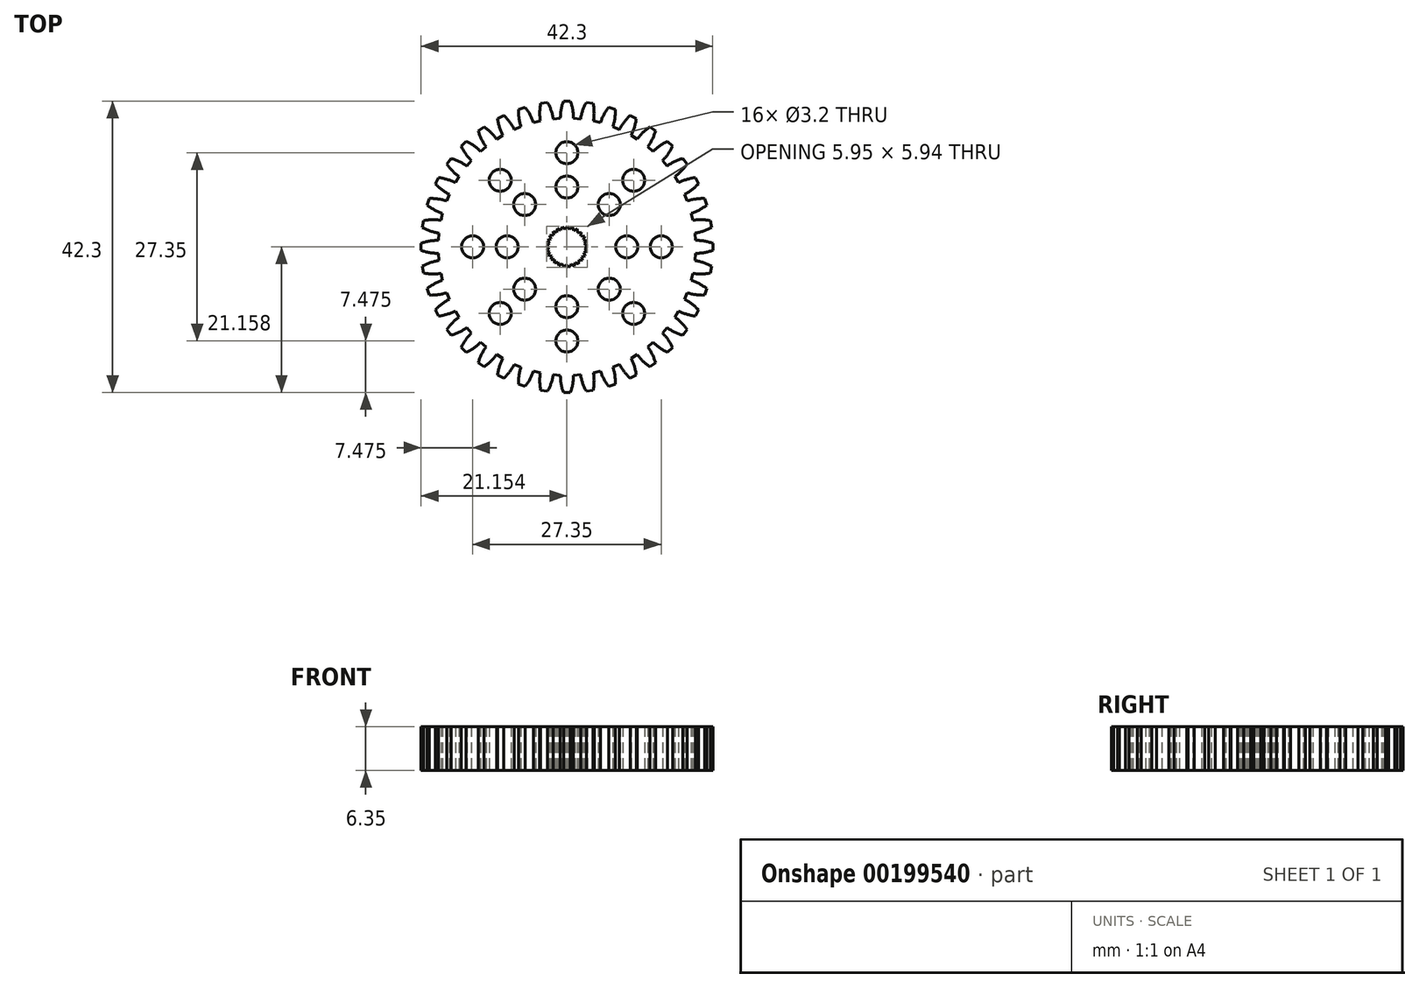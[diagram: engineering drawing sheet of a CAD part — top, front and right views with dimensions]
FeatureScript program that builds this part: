
annotation { "Feature Type Name" : "Feature", "Feature Type Description" : "" }
export const myFeature = defineFeature(function(context is Context, id is Id, definition is map)
    precondition{}
    {
        {
            var Q0;
            Q0=qCreatedBy(makeId("Top.planeOp"),FACE);
            var sketch = newSketch(context, id + "F0", { "sketchPlane" : qUnion([Q0])});
            skLineSegment(sketch, "E0", {"start": v(-0.5, 21.15) * mm, "end": v(0.5, 21.15) * mm});
            skArc(sketch, "E1", {"start": v(-0.5, 21.15) * mm, "mid": v(-0.84, 19.92) * mm, "end": v(-0.95, 18.65) * mm});
            skArc(sketch, "E2.MirrorCS", {"start": v(0.5, 21.15) * mm, "mid": v(0.84, 19.92) * mm, "end": v(0.95, 18.65) * mm});
            skArc(sketch, "E3.1.0", {"start": v(-2.81, 20.97) * mm, "mid": v(-2.3, 19.8) * mm, "end": v(-1.98, 18.57) * mm});
            skLineSegment(sketch, "E3.1.1", {"start": v(-3.8, 20.81) * mm, "end": v(-2.81, 20.97) * mm});
            skArc(sketch, "E3.1.2", {"start": v(-3.8, 20.81) * mm, "mid": v(-3.94, 19.54) * mm, "end": v(-3.86, 18.27) * mm});
            skArc(sketch, "E3.2.0", {"start": v(-6.06, 20.27) * mm, "mid": v(-5.36, 19.2) * mm, "end": v(-4.86, 18.03) * mm});
            skLineSegment(sketch, "E3.2.1", {"start": v(-7.01, 19.96) * mm, "end": v(-6.06, 20.27) * mm});
            skArc(sketch, "E3.2.2", {"start": v(-7.01, 19.96) * mm, "mid": v(-6.95, 18.69) * mm, "end": v(-6.67, 17.44) * mm});
            skArc(sketch, "E3.3.0", {"start": v(-9.16, 19.07) * mm, "mid": v(-8.3, 18.13) * mm, "end": v(-7.62, 17.05) * mm});
            skLineSegment(sketch, "E3.3.1", {"start": v(-10.05, 18.62) * mm, "end": v(-9.16, 19.07) * mm});
            skArc(sketch, "E3.3.2", {"start": v(-10.05, 18.62) * mm, "mid": v(-9.79, 17.37) * mm, "end": v(-9.31, 16.19) * mm});
            skArc(sketch, "E3.4.0", {"start": v(-12.03, 17.4) * mm, "mid": v(-11.03, 16.6) * mm, "end": v(-10.2, 15.65) * mm});
            skLineSegment(sketch, "E3.4.1", {"start": v(-12.84, 16.82) * mm, "end": v(-12.03, 17.4) * mm});
            skArc(sketch, "E3.4.2", {"start": v(-12.84, 16.82) * mm, "mid": v(-12.39, 15.62) * mm, "end": v(-11.73, 14.53) * mm});
            skArc(sketch, "E3.5.0", {"start": v(-14.6, 15.3) * mm, "mid": v(-13.5, 14.68) * mm, "end": v(-12.52, 13.86) * mm});
            skLineSegment(sketch, "E3.5.1", {"start": v(-15.3, 14.6) * mm, "end": v(-14.6, 15.3) * mm});
            skArc(sketch, "E3.5.2", {"start": v(-15.3, 14.6) * mm, "mid": v(-14.68, 13.5) * mm, "end": v(-13.86, 12.52) * mm});
            skArc(sketch, "E3.6.0", {"start": v(-16.82, 12.84) * mm, "mid": v(-15.62, 12.39) * mm, "end": v(-14.53, 11.73) * mm});
            skLineSegment(sketch, "E3.6.1", {"start": v(-17.4, 12.03) * mm, "end": v(-16.82, 12.84) * mm});
            skArc(sketch, "E3.6.2", {"start": v(-17.4, 12.03) * mm, "mid": v(-16.6, 11.03) * mm, "end": v(-15.65, 10.2) * mm});
            skArc(sketch, "E3.7.0", {"start": v(-18.62, 10.05) * mm, "mid": v(-17.37, 9.79) * mm, "end": v(-16.19, 9.31) * mm});
            skLineSegment(sketch, "E3.7.1", {"start": v(-19.07, 9.16) * mm, "end": v(-18.62, 10.05) * mm});
            skArc(sketch, "E3.7.2", {"start": v(-19.07, 9.16) * mm, "mid": v(-18.13, 8.3) * mm, "end": v(-17.05, 7.62) * mm});
            skArc(sketch, "E3.8.0", {"start": v(-19.96, 7.01) * mm, "mid": v(-18.69, 6.95) * mm, "end": v(-17.44, 6.67) * mm});
            skLineSegment(sketch, "E3.8.1", {"start": v(-20.27, 6.06) * mm, "end": v(-19.96, 7.01) * mm});
            skArc(sketch, "E3.8.2", {"start": v(-20.27, 6.06) * mm, "mid": v(-19.2, 5.36) * mm, "end": v(-18.03, 4.86) * mm});
            skArc(sketch, "E3.9.0", {"start": v(-20.81, 3.8) * mm, "mid": v(-19.54, 3.94) * mm, "end": v(-18.27, 3.86) * mm});
            skLineSegment(sketch, "E3.9.1", {"start": v(-20.97, 2.81) * mm, "end": v(-20.81, 3.8) * mm});
            skArc(sketch, "E3.9.2", {"start": v(-20.97, 2.81) * mm, "mid": v(-19.8, 2.3) * mm, "end": v(-18.57, 1.98) * mm});
            skArc(sketch, "E3.10.0", {"start": v(-21.15, 0.5) * mm, "mid": v(-19.92, 0.84) * mm, "end": v(-18.65, 0.95) * mm});
            skLineSegment(sketch, "E3.10.1", {"start": v(-21.15, -0.5) * mm, "end": v(-21.15, 0.5) * mm});
            skArc(sketch, "E3.10.2", {"start": v(-21.15, -0.5) * mm, "mid": v(-19.92, -0.84) * mm, "end": v(-18.65, -0.95) * mm});
            skArc(sketch, "E3.11.0", {"start": v(-20.97, -2.81) * mm, "mid": v(-19.8, -2.3) * mm, "end": v(-18.57, -1.98) * mm});
            skLineSegment(sketch, "E3.11.1", {"start": v(-20.81, -3.8) * mm, "end": v(-20.97, -2.81) * mm});
            skArc(sketch, "E3.11.2", {"start": v(-20.81, -3.8) * mm, "mid": v(-19.54, -3.94) * mm, "end": v(-18.27, -3.86) * mm});
            skArc(sketch, "E3.12.0", {"start": v(-20.27, -6.06) * mm, "mid": v(-19.2, -5.36) * mm, "end": v(-18.03, -4.86) * mm});
            skLineSegment(sketch, "E3.12.1", {"start": v(-19.96, -7.01) * mm, "end": v(-20.27, -6.06) * mm});
            skArc(sketch, "E3.12.2", {"start": v(-19.96, -7.01) * mm, "mid": v(-18.69, -6.95) * mm, "end": v(-17.44, -6.67) * mm});
            skArc(sketch, "E3.13.0", {"start": v(-19.07, -9.16) * mm, "mid": v(-18.13, -8.3) * mm, "end": v(-17.05, -7.62) * mm});
            skLineSegment(sketch, "E3.13.1", {"start": v(-18.62, -10.05) * mm, "end": v(-19.07, -9.16) * mm});
            skArc(sketch, "E3.13.2", {"start": v(-18.62, -10.05) * mm, "mid": v(-17.37, -9.79) * mm, "end": v(-16.19, -9.31) * mm});
            skArc(sketch, "E3.14.0", {"start": v(-17.4, -12.03) * mm, "mid": v(-16.6, -11.03) * mm, "end": v(-15.65, -10.2) * mm});
            skLineSegment(sketch, "E3.14.1", {"start": v(-16.82, -12.84) * mm, "end": v(-17.4, -12.03) * mm});
            skArc(sketch, "E3.14.2", {"start": v(-16.82, -12.84) * mm, "mid": v(-15.62, -12.39) * mm, "end": v(-14.53, -11.73) * mm});
            skArc(sketch, "E3.15.0", {"start": v(-15.3, -14.6) * mm, "mid": v(-14.68, -13.5) * mm, "end": v(-13.86, -12.52) * mm});
            skLineSegment(sketch, "E3.15.1", {"start": v(-14.6, -15.3) * mm, "end": v(-15.3, -14.6) * mm});
            skArc(sketch, "E3.15.2", {"start": v(-14.6, -15.3) * mm, "mid": v(-13.5, -14.68) * mm, "end": v(-12.52, -13.86) * mm});
            skArc(sketch, "E3.16.0", {"start": v(-12.84, -16.82) * mm, "mid": v(-12.39, -15.62) * mm, "end": v(-11.73, -14.53) * mm});
            skLineSegment(sketch, "E3.16.1", {"start": v(-12.03, -17.4) * mm, "end": v(-12.84, -16.82) * mm});
            skArc(sketch, "E3.16.2", {"start": v(-12.03, -17.4) * mm, "mid": v(-11.03, -16.6) * mm, "end": v(-10.2, -15.65) * mm});
            skArc(sketch, "E3.17.0", {"start": v(-10.05, -18.62) * mm, "mid": v(-9.79, -17.37) * mm, "end": v(-9.31, -16.19) * mm});
            skLineSegment(sketch, "E3.17.1", {"start": v(-9.16, -19.07) * mm, "end": v(-10.05, -18.62) * mm});
            skArc(sketch, "E3.17.2", {"start": v(-9.16, -19.07) * mm, "mid": v(-8.3, -18.13) * mm, "end": v(-7.62, -17.05) * mm});
            skArc(sketch, "E3.18.0", {"start": v(-7.01, -19.96) * mm, "mid": v(-6.95, -18.69) * mm, "end": v(-6.67, -17.44) * mm});
            skLineSegment(sketch, "E3.18.1", {"start": v(-6.06, -20.27) * mm, "end": v(-7.01, -19.96) * mm});
            skArc(sketch, "E3.18.2", {"start": v(-6.06, -20.27) * mm, "mid": v(-5.36, -19.2) * mm, "end": v(-4.86, -18.03) * mm});
            skArc(sketch, "E3.19.0", {"start": v(-3.8, -20.81) * mm, "mid": v(-3.94, -19.54) * mm, "end": v(-3.86, -18.27) * mm});
            skLineSegment(sketch, "E3.19.1", {"start": v(-2.81, -20.97) * mm, "end": v(-3.8, -20.81) * mm});
            skArc(sketch, "E3.19.2", {"start": v(-2.81, -20.97) * mm, "mid": v(-2.3, -19.8) * mm, "end": v(-1.98, -18.57) * mm});
            skArc(sketch, "E3.20.0", {"start": v(-0.5, -21.15) * mm, "mid": v(-0.84, -19.92) * mm, "end": v(-0.95, -18.65) * mm});
            skLineSegment(sketch, "E3.20.1", {"start": v(0.5, -21.15) * mm, "end": v(-0.5, -21.15) * mm});
            skArc(sketch, "E3.20.2", {"start": v(0.5, -21.15) * mm, "mid": v(0.84, -19.92) * mm, "end": v(0.95, -18.65) * mm});
            skArc(sketch, "E3.21.0", {"start": v(2.81, -20.97) * mm, "mid": v(2.3, -19.8) * mm, "end": v(1.98, -18.57) * mm});
            skLineSegment(sketch, "E3.21.1", {"start": v(3.8, -20.81) * mm, "end": v(2.81, -20.97) * mm});
            skArc(sketch, "E3.21.2", {"start": v(3.8, -20.81) * mm, "mid": v(3.94, -19.54) * mm, "end": v(3.86, -18.27) * mm});
            skArc(sketch, "E3.22.0", {"start": v(6.06, -20.27) * mm, "mid": v(5.36, -19.2) * mm, "end": v(4.86, -18.03) * mm});
            skLineSegment(sketch, "E3.22.1", {"start": v(7.01, -19.96) * mm, "end": v(6.06, -20.27) * mm});
            skArc(sketch, "E3.22.2", {"start": v(7.01, -19.96) * mm, "mid": v(6.95, -18.69) * mm, "end": v(6.67, -17.44) * mm});
            skArc(sketch, "E3.23.0", {"start": v(9.16, -19.07) * mm, "mid": v(8.3, -18.13) * mm, "end": v(7.62, -17.05) * mm});
            skLineSegment(sketch, "E3.23.1", {"start": v(10.05, -18.62) * mm, "end": v(9.16, -19.07) * mm});
            skArc(sketch, "E3.23.2", {"start": v(10.05, -18.62) * mm, "mid": v(9.79, -17.37) * mm, "end": v(9.31, -16.19) * mm});
            skArc(sketch, "E3.24.0", {"start": v(12.03, -17.4) * mm, "mid": v(11.03, -16.6) * mm, "end": v(10.2, -15.65) * mm});
            skLineSegment(sketch, "E3.24.1", {"start": v(12.84, -16.82) * mm, "end": v(12.03, -17.4) * mm});
            skArc(sketch, "E3.24.2", {"start": v(12.84, -16.82) * mm, "mid": v(12.39, -15.62) * mm, "end": v(11.73, -14.53) * mm});
            skArc(sketch, "E3.25.0", {"start": v(14.6, -15.3) * mm, "mid": v(13.5, -14.68) * mm, "end": v(12.52, -13.86) * mm});
            skLineSegment(sketch, "E3.25.1", {"start": v(15.3, -14.6) * mm, "end": v(14.6, -15.3) * mm});
            skArc(sketch, "E3.25.2", {"start": v(15.3, -14.6) * mm, "mid": v(14.68, -13.5) * mm, "end": v(13.86, -12.52) * mm});
            skArc(sketch, "E3.26.0", {"start": v(16.82, -12.84) * mm, "mid": v(15.62, -12.39) * mm, "end": v(14.53, -11.73) * mm});
            skLineSegment(sketch, "E3.26.1", {"start": v(17.4, -12.03) * mm, "end": v(16.82, -12.84) * mm});
            skArc(sketch, "E3.26.2", {"start": v(17.4, -12.03) * mm, "mid": v(16.6, -11.03) * mm, "end": v(15.65, -10.2) * mm});
            skArc(sketch, "E3.27.0", {"start": v(18.62, -10.05) * mm, "mid": v(17.37, -9.79) * mm, "end": v(16.19, -9.31) * mm});
            skLineSegment(sketch, "E3.27.1", {"start": v(19.07, -9.16) * mm, "end": v(18.62, -10.05) * mm});
            skArc(sketch, "E3.27.2", {"start": v(19.07, -9.16) * mm, "mid": v(18.13, -8.3) * mm, "end": v(17.05, -7.62) * mm});
            skArc(sketch, "E3.28.0", {"start": v(19.96, -7.01) * mm, "mid": v(18.69, -6.95) * mm, "end": v(17.44, -6.67) * mm});
            skLineSegment(sketch, "E3.28.1", {"start": v(20.27, -6.06) * mm, "end": v(19.96, -7.01) * mm});
            skArc(sketch, "E3.28.2", {"start": v(20.27, -6.06) * mm, "mid": v(19.2, -5.36) * mm, "end": v(18.03, -4.86) * mm});
            skArc(sketch, "E3.29.0", {"start": v(20.81, -3.8) * mm, "mid": v(19.54, -3.94) * mm, "end": v(18.27, -3.86) * mm});
            skLineSegment(sketch, "E3.29.1", {"start": v(20.97, -2.81) * mm, "end": v(20.81, -3.8) * mm});
            skArc(sketch, "E3.29.2", {"start": v(20.97, -2.81) * mm, "mid": v(19.8, -2.3) * mm, "end": v(18.57, -1.98) * mm});
            skArc(sketch, "E3.30.0", {"start": v(21.15, -0.5) * mm, "mid": v(19.92, -0.84) * mm, "end": v(18.65, -0.95) * mm});
            skLineSegment(sketch, "E3.30.1", {"start": v(21.15, 0.5) * mm, "end": v(21.15, -0.5) * mm});
            skArc(sketch, "E3.30.2", {"start": v(21.15, 0.5) * mm, "mid": v(19.92, 0.84) * mm, "end": v(18.65, 0.95) * mm});
            skArc(sketch, "E3.31.0", {"start": v(20.97, 2.81) * mm, "mid": v(19.8, 2.3) * mm, "end": v(18.57, 1.98) * mm});
            skLineSegment(sketch, "E3.31.1", {"start": v(20.81, 3.8) * mm, "end": v(20.97, 2.81) * mm});
            skArc(sketch, "E3.31.2", {"start": v(20.81, 3.8) * mm, "mid": v(19.54, 3.94) * mm, "end": v(18.27, 3.86) * mm});
            skArc(sketch, "E3.32.0", {"start": v(20.27, 6.06) * mm, "mid": v(19.2, 5.36) * mm, "end": v(18.03, 4.86) * mm});
            skLineSegment(sketch, "E3.32.1", {"start": v(19.96, 7.01) * mm, "end": v(20.27, 6.06) * mm});
            skArc(sketch, "E3.32.2", {"start": v(19.96, 7.01) * mm, "mid": v(18.69, 6.95) * mm, "end": v(17.44, 6.67) * mm});
            skArc(sketch, "E3.33.0", {"start": v(19.07, 9.16) * mm, "mid": v(18.13, 8.3) * mm, "end": v(17.05, 7.62) * mm});
            skLineSegment(sketch, "E3.33.1", {"start": v(18.62, 10.05) * mm, "end": v(19.07, 9.16) * mm});
            skArc(sketch, "E3.33.2", {"start": v(18.62, 10.05) * mm, "mid": v(17.37, 9.79) * mm, "end": v(16.19, 9.31) * mm});
            skArc(sketch, "E3.34.0", {"start": v(17.4, 12.03) * mm, "mid": v(16.6, 11.03) * mm, "end": v(15.65, 10.2) * mm});
            skLineSegment(sketch, "E3.34.1", {"start": v(16.82, 12.84) * mm, "end": v(17.4, 12.03) * mm});
            skArc(sketch, "E3.34.2", {"start": v(16.82, 12.84) * mm, "mid": v(15.62, 12.39) * mm, "end": v(14.53, 11.73) * mm});
            skArc(sketch, "E3.35.0", {"start": v(15.3, 14.6) * mm, "mid": v(14.68, 13.5) * mm, "end": v(13.86, 12.52) * mm});
            skLineSegment(sketch, "E3.35.1", {"start": v(14.6, 15.3) * mm, "end": v(15.3, 14.6) * mm});
            skArc(sketch, "E3.35.2", {"start": v(14.6, 15.3) * mm, "mid": v(13.5, 14.68) * mm, "end": v(12.52, 13.86) * mm});
            skArc(sketch, "E3.36.0", {"start": v(12.84, 16.82) * mm, "mid": v(12.39, 15.62) * mm, "end": v(11.73, 14.53) * mm});
            skLineSegment(sketch, "E3.36.1", {"start": v(12.03, 17.4) * mm, "end": v(12.84, 16.82) * mm});
            skArc(sketch, "E3.36.2", {"start": v(12.03, 17.4) * mm, "mid": v(11.03, 16.6) * mm, "end": v(10.2, 15.65) * mm});
            skArc(sketch, "E3.37.0", {"start": v(10.05, 18.62) * mm, "mid": v(9.79, 17.37) * mm, "end": v(9.31, 16.19) * mm});
            skLineSegment(sketch, "E3.37.1", {"start": v(9.16, 19.07) * mm, "end": v(10.05, 18.62) * mm});
            skArc(sketch, "E3.37.2", {"start": v(9.16, 19.07) * mm, "mid": v(8.3, 18.13) * mm, "end": v(7.62, 17.05) * mm});
            skArc(sketch, "E3.38.0", {"start": v(7.01, 19.96) * mm, "mid": v(6.95, 18.69) * mm, "end": v(6.67, 17.44) * mm});
            skLineSegment(sketch, "E3.38.1", {"start": v(6.06, 20.27) * mm, "end": v(7.01, 19.96) * mm});
            skArc(sketch, "E3.38.2", {"start": v(6.06, 20.27) * mm, "mid": v(5.36, 19.2) * mm, "end": v(4.86, 18.03) * mm});
            skArc(sketch, "E3.39.0", {"start": v(3.8, 20.81) * mm, "mid": v(3.94, 19.54) * mm, "end": v(3.86, 18.27) * mm});
            skLineSegment(sketch, "E3.39.1", {"start": v(2.81, 20.97) * mm, "end": v(3.8, 20.81) * mm});
            skArc(sketch, "E3.39.2", {"start": v(2.81, 20.97) * mm, "mid": v(2.3, 19.8) * mm, "end": v(1.98, 18.57) * mm});
            skPoint(sketch, "E3.center", {"position": v(0, 0) * mm});
            skLineSegment(sketch, "E4", {"start": v(-2.48, 1.65) * mm, "end": v(-2.31, 1.15) * mm});
            skLineSegment(sketch, "E5", {"start": v(-2.31, 1.15) * mm, "end": v(-2.81, 0.98) * mm});
            skLineSegment(sketch, "E6.1.0", {"start": v(-2.81, 0.98) * mm, "end": v(-2.53, 0.54) * mm});
            skLineSegment(sketch, "E6.1.1", {"start": v(-2.53, 0.54) * mm, "end": v(-2.97, 0.25) * mm});
            skLineSegment(sketch, "E6.2.0", {"start": v(-2.97, 0.25) * mm, "end": v(-2.58, -0.1) * mm});
            skLineSegment(sketch, "E6.2.1", {"start": v(-2.58, -0.1) * mm, "end": v(-2.94, -0.5) * mm});
            skLineSegment(sketch, "E6.3.0", {"start": v(-2.94, -0.5) * mm, "end": v(-2.47, -0.74) * mm});
            skLineSegment(sketch, "E6.3.1", {"start": v(-2.47, -0.74) * mm, "end": v(-2.72, -1.2) * mm});
            skLineSegment(sketch, "E6.4.0", {"start": v(-2.72, -1.2) * mm, "end": v(-2.21, -1.34) * mm});
            skLineSegment(sketch, "E6.4.1", {"start": v(-2.21, -1.34) * mm, "end": v(-2.34, -1.85) * mm});
            skLineSegment(sketch, "E6.5.0", {"start": v(-2.34, -1.85) * mm, "end": v(-1.8, -1.84) * mm});
            skLineSegment(sketch, "E6.5.1", {"start": v(-1.8, -1.84) * mm, "end": v(-1.8, -2.37) * mm});
            skLineSegment(sketch, "E6.6.0", {"start": v(-1.8, -2.37) * mm, "end": v(-1.3, -2.24) * mm});
            skLineSegment(sketch, "E6.6.1", {"start": v(-1.3, -2.24) * mm, "end": v(-1.16, -2.75) * mm});
            skLineSegment(sketch, "E6.7.0", {"start": v(-1.16, -2.75) * mm, "end": v(-0.7, -2.49) * mm});
            skLineSegment(sketch, "E6.7.1", {"start": v(-0.7, -2.49) * mm, "end": v(-0.44, -2.95) * mm});
            skLineSegment(sketch, "E6.8.0", {"start": v(-0.44, -2.95) * mm, "end": v(-0.06, -2.58) * mm});
            skLineSegment(sketch, "E6.8.1", {"start": v(-0.06, -2.58) * mm, "end": v(0.3, -2.96) * mm});
            skLineSegment(sketch, "E6.9.0", {"start": v(0.3, -2.96) * mm, "end": v(0.59, -2.52) * mm});
            skLineSegment(sketch, "E6.9.1", {"start": v(0.59, -2.52) * mm, "end": v(1.04, -2.8) * mm});
            skLineSegment(sketch, "E6.10.0", {"start": v(1.04, -2.8) * mm, "end": v(1.2, -2.3) * mm});
            skLineSegment(sketch, "E6.10.1", {"start": v(1.2, -2.3) * mm, "end": v(1.7, -2.45) * mm});
            skLineSegment(sketch, "E6.11.0", {"start": v(1.7, -2.45) * mm, "end": v(1.73, -1.92) * mm});
            skLineSegment(sketch, "E6.11.1", {"start": v(1.73, -1.92) * mm, "end": v(2.25, -1.95) * mm});
            skLineSegment(sketch, "E6.12.0", {"start": v(2.25, -1.95) * mm, "end": v(2.15, -1.43) * mm});
            skLineSegment(sketch, "E6.12.1", {"start": v(2.15, -1.43) * mm, "end": v(2.67, -1.33) * mm});
            skLineSegment(sketch, "E6.13.0", {"start": v(2.67, -1.33) * mm, "end": v(2.44, -0.85) * mm});
            skLineSegment(sketch, "E6.13.1", {"start": v(2.44, -0.85) * mm, "end": v(2.91, -0.62) * mm});
            skLineSegment(sketch, "E6.14.0", {"start": v(2.91, -0.62) * mm, "end": v(2.57, -0.22) * mm});
            skLineSegment(sketch, "E6.14.1", {"start": v(2.57, -0.22) * mm, "end": v(2.98, 0.12) * mm});
            skLineSegment(sketch, "E6.15.0", {"start": v(2.98, 0.12) * mm, "end": v(2.55, 0.43) * mm});
            skLineSegment(sketch, "E6.15.1", {"start": v(2.55, 0.43) * mm, "end": v(2.85, 0.86) * mm});
            skLineSegment(sketch, "E6.16.0", {"start": v(2.85, 0.86) * mm, "end": v(2.36, 1.05) * mm});
            skLineSegment(sketch, "E6.16.1", {"start": v(2.36, 1.05) * mm, "end": v(2.55, 1.54) * mm});
            skLineSegment(sketch, "E6.17.0", {"start": v(2.55, 1.54) * mm, "end": v(2.03, 1.6) * mm});
            skLineSegment(sketch, "E6.17.1", {"start": v(2.03, 1.6) * mm, "end": v(2.09, 2.13) * mm});
            skLineSegment(sketch, "E6.18.0", {"start": v(2.09, 2.13) * mm, "end": v(1.56, 2.06) * mm});
            skLineSegment(sketch, "E6.18.1", {"start": v(1.56, 2.06) * mm, "end": v(1.5, 2.58) * mm});
            skLineSegment(sketch, "E6.19.0", {"start": v(1.5, 2.58) * mm, "end": v(1, 2.38) * mm});
            skLineSegment(sketch, "E6.19.1", {"start": v(1, 2.38) * mm, "end": v(0.8, 2.87) * mm});
            skLineSegment(sketch, "E6.20.0", {"start": v(0.8, 2.87) * mm, "end": v(0.38, 2.56) * mm});
            skLineSegment(sketch, "E6.20.1", {"start": v(0.38, 2.56) * mm, "end": v(0.07, 2.98) * mm});
            skLineSegment(sketch, "E6.21.0", {"start": v(0.07, 2.98) * mm, "end": v(-0.27, 2.57) * mm});
            skLineSegment(sketch, "E6.21.1", {"start": v(-0.27, 2.57) * mm, "end": v(-0.68, 2.9) * mm});
            skLineSegment(sketch, "E6.22.0", {"start": v(-0.68, 2.9) * mm, "end": v(-0.9, 2.42) * mm});
            skLineSegment(sketch, "E6.22.1", {"start": v(-0.9, 2.42) * mm, "end": v(-1.38, 2.64) * mm});
            skLineSegment(sketch, "E6.23.0", {"start": v(-1.38, 2.64) * mm, "end": v(-1.47, 2.12) * mm});
            skLineSegment(sketch, "E6.23.1", {"start": v(-1.47, 2.12) * mm, "end": v(-2, 2.22) * mm});
            skLineSegment(sketch, "E6.24.0", {"start": v(-2, 2.22) * mm, "end": v(-1.95, 1.69) * mm});
            skLineSegment(sketch, "E6.24.1", {"start": v(-1.95, 1.69) * mm, "end": v(-2.48, 1.65) * mm});
            skCircle(sketch, "E7", {"center": v(0, 13.67) * mm, "radius": 1.6 * mm});
            skCircle(sketch, "E8", {"center": v(0, 8.67) * mm, "radius": 1.6 * mm});
            skLineSegment(sketch, "E9", {"start": v(0, 13.67) * mm, "end": v(0, 7.54) * mm});
            skCircle(sketch, "E10.1.0", {"center": v(-9.67, 9.67) * mm, "radius": 1.6 * mm});
            skCircle(sketch, "E10.1.1", {"center": v(-6.13, 6.13) * mm, "radius": 1.6 * mm});
            skCircle(sketch, "E10.2.0", {"center": v(-13.67, 0) * mm, "radius": 1.6 * mm});
            skCircle(sketch, "E10.2.1", {"center": v(-8.67, 0) * mm, "radius": 1.6 * mm});
            skCircle(sketch, "E10.3.0", {"center": v(-9.67, -9.67) * mm, "radius": 1.6 * mm});
            skCircle(sketch, "E10.3.1", {"center": v(-6.13, -6.13) * mm, "radius": 1.6 * mm});
            skCircle(sketch, "E10.4.0", {"center": v(0, -13.67) * mm, "radius": 1.6 * mm});
            skCircle(sketch, "E10.4.1", {"center": v(0, -8.67) * mm, "radius": 1.6 * mm});
            skCircle(sketch, "E10.5.0", {"center": v(9.67, -9.67) * mm, "radius": 1.6 * mm});
            skCircle(sketch, "E10.5.1", {"center": v(6.13, -6.13) * mm, "radius": 1.6 * mm});
            skCircle(sketch, "E10.6.0", {"center": v(13.67, 0) * mm, "radius": 1.6 * mm});
            skCircle(sketch, "E10.6.1", {"center": v(8.67, 0) * mm, "radius": 1.6 * mm});
            skCircle(sketch, "E10.7.0", {"center": v(9.67, 9.67) * mm, "radius": 1.6 * mm});
            skCircle(sketch, "E10.7.1", {"center": v(6.13, 6.13) * mm, "radius": 1.6 * mm});
            skLineSegment(sketch, "E11", {"start": v(0.95, 18.65) * mm, "end": v(1.98, 18.57) * mm});
            skLineSegment(sketch, "E12.1.0", {"start": v(-1.98, 18.57) * mm, "end": v(-0.95, 18.65) * mm});
            skLineSegment(sketch, "E12.2.0", {"start": v(-4.86, 18.03) * mm, "end": v(-3.86, 18.27) * mm});
            skLineSegment(sketch, "E12.3.0", {"start": v(-7.62, 17.05) * mm, "end": v(-6.67, 17.44) * mm});
            skLineSegment(sketch, "E12.4.0", {"start": v(-10.2, 15.65) * mm, "end": v(-9.31, 16.19) * mm});
            skLineSegment(sketch, "E12.5.0", {"start": v(-12.52, 13.86) * mm, "end": v(-11.73, 14.53) * mm});
            skLineSegment(sketch, "E12.6.0", {"start": v(-14.53, 11.73) * mm, "end": v(-13.86, 12.52) * mm});
            skLineSegment(sketch, "E12.7.0", {"start": v(-16.19, 9.31) * mm, "end": v(-15.65, 10.2) * mm});
            skLineSegment(sketch, "E12.8.0", {"start": v(-17.44, 6.67) * mm, "end": v(-17.05, 7.62) * mm});
            skLineSegment(sketch, "E12.9.0", {"start": v(-18.27, 3.86) * mm, "end": v(-18.03, 4.86) * mm});
            skLineSegment(sketch, "E12.10.0", {"start": v(-18.65, 0.95) * mm, "end": v(-18.57, 1.98) * mm});
            skLineSegment(sketch, "E12.11.0", {"start": v(-18.57, -1.98) * mm, "end": v(-18.65, -0.95) * mm});
            skLineSegment(sketch, "E12.12.0", {"start": v(-18.03, -4.86) * mm, "end": v(-18.27, -3.86) * mm});
            skLineSegment(sketch, "E12.13.0", {"start": v(-17.05, -7.62) * mm, "end": v(-17.44, -6.67) * mm});
            skLineSegment(sketch, "E12.14.0", {"start": v(-15.65, -10.2) * mm, "end": v(-16.19, -9.31) * mm});
            skLineSegment(sketch, "E12.15.0", {"start": v(-13.86, -12.52) * mm, "end": v(-14.53, -11.73) * mm});
            skLineSegment(sketch, "E12.16.0", {"start": v(-11.73, -14.53) * mm, "end": v(-12.52, -13.86) * mm});
            skLineSegment(sketch, "E12.17.0", {"start": v(-9.31, -16.19) * mm, "end": v(-10.2, -15.65) * mm});
            skLineSegment(sketch, "E12.18.0", {"start": v(-6.67, -17.44) * mm, "end": v(-7.62, -17.05) * mm});
            skLineSegment(sketch, "E12.19.0", {"start": v(-3.86, -18.27) * mm, "end": v(-4.86, -18.03) * mm});
            skLineSegment(sketch, "E12.20.0", {"start": v(-0.95, -18.65) * mm, "end": v(-1.98, -18.57) * mm});
            skLineSegment(sketch, "E12.21.0", {"start": v(1.98, -18.57) * mm, "end": v(0.95, -18.65) * mm});
            skLineSegment(sketch, "E12.22.0", {"start": v(4.86, -18.03) * mm, "end": v(3.86, -18.27) * mm});
            skLineSegment(sketch, "E12.23.0", {"start": v(7.62, -17.05) * mm, "end": v(6.67, -17.44) * mm});
            skLineSegment(sketch, "E12.24.0", {"start": v(10.2, -15.65) * mm, "end": v(9.31, -16.19) * mm});
            skLineSegment(sketch, "E12.25.0", {"start": v(12.52, -13.86) * mm, "end": v(11.73, -14.53) * mm});
            skLineSegment(sketch, "E12.26.0", {"start": v(14.53, -11.73) * mm, "end": v(13.86, -12.52) * mm});
            skLineSegment(sketch, "E12.27.0", {"start": v(16.19, -9.31) * mm, "end": v(15.65, -10.2) * mm});
            skLineSegment(sketch, "E12.28.0", {"start": v(17.44, -6.67) * mm, "end": v(17.05, -7.62) * mm});
            skLineSegment(sketch, "E12.29.0", {"start": v(18.27, -3.86) * mm, "end": v(18.03, -4.86) * mm});
            skLineSegment(sketch, "E12.30.0", {"start": v(18.65, -0.95) * mm, "end": v(18.57, -1.98) * mm});
            skLineSegment(sketch, "E12.31.0", {"start": v(18.57, 1.98) * mm, "end": v(18.65, 0.95) * mm});
            skLineSegment(sketch, "E12.32.0", {"start": v(18.03, 4.86) * mm, "end": v(18.27, 3.86) * mm});
            skLineSegment(sketch, "E12.33.0", {"start": v(17.05, 7.62) * mm, "end": v(17.44, 6.67) * mm});
            skLineSegment(sketch, "E12.34.0", {"start": v(15.65, 10.2) * mm, "end": v(16.19, 9.31) * mm});
            skLineSegment(sketch, "E12.35.0", {"start": v(13.86, 12.52) * mm, "end": v(14.53, 11.73) * mm});
            skLineSegment(sketch, "E12.36.0", {"start": v(11.73, 14.53) * mm, "end": v(12.52, 13.86) * mm});
            skLineSegment(sketch, "E12.37.0", {"start": v(9.31, 16.19) * mm, "end": v(10.2, 15.65) * mm});
            skLineSegment(sketch, "E12.38.0", {"start": v(6.67, 17.44) * mm, "end": v(7.62, 17.05) * mm});
            skLineSegment(sketch, "E12.39.0", {"start": v(3.86, 18.27) * mm, "end": v(4.86, 18.03) * mm});
            skSolve(sketch);
        }
        {
            var Q0;
            Q0=makeQuery(id+"F0.imprint","IMPRINT",FACE,{"disambiguationData":[TD([[makeQuery(id+"F0.imprint","IMPRINT",EDGE,{"derivedFrom":sQuery(id+"F0.wireOp",EDGE,"E0")}),-1.0]])]});
            extrude(context, id + "F1", {"entities" : qUnion([Q0]), "depth" : 6.35 * mm});
        }
    });
